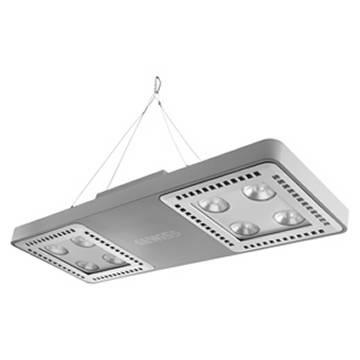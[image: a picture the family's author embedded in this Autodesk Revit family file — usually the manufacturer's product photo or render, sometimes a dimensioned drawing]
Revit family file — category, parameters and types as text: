
# Revit family: Lighting-Industrial-GEWISS-SMART[4]HE_HIGHBAYS-LED_2M_DALI
name_source: partatom
category: Apparecchi per illuminazione
units: mm (PartAtom-declared; Revit-internal decimal feet)

## family parameters
Basato su piano di lavoro = Sì
Condiviso = No
Numero OmniClass = 23.80.70.00
Punto di calcolo locali = No
Quota connettore circolare = Usa diametro
Sempre verticale = No
Sorgente d'illuminazione = No
Taglio con vuoti quando caricato = No
Tipo di parte = Normale
Titolo OmniClass = Lighting

## types (36) — shared parameters
Application = Internal
Body = PA6 "Halogen Free" loaded fibreglass
Carico apparente = 97 VA
Catalogue = LIGHTING
Classification: = -
Classificazione = Lighting
Color Rendering Index = CRI-80
Colour = Grey RAL 7035
Colour : = Grey RAL 7035
Commenti sul wattaggio = 97W
Context = Lighting for industries and sports facilities
Control System = 1 x DALI DT6
Control System : = DALI
DIN 18032-3 certification = With Bracket - Rope Kit + terminal&nbsp;(in approval)
Device with reduced surface temperature = Yes
Dist_sorg_lum = 10 mm  [stored 0.0328084 ft]
Driver = Included
Driver Box = Built-in
Electrocod = 2444
Eletrical and lighting features = -
External screw = Stainless steel
Fixing = -
Gasket = anti-aging silicone
General information = -
Glow Wire Test : = 850 °C
IDF = 71863346-6837-4260-98ca-c6d85b474ae1
IDT = 32167967fdf74962832821affbd5ec12
IP degree = IP66
IPEA = -
Immagine tipo = GWL1311.jpg
Installationa and maintenance = -
Insulation class = I
LED Maintenance = Non-replaceable
Lampada = LED
Larghezza = 254 mm
Lifetime = L90B10 (Tq+25°C) = 100.000 h - L90B10 (Tq+50°C) = 50.000 h
Locking Hook = -
Luminaire = LED Industrial ReflectorÂ
Lunghezza = 699 mm  [stored 2.29331 ft]
Mascherina = <Per categoria>
Materials = -
Maximum surface exposed to the wind : = 0,184 m²
Motore = <Per categoria>
Mouting and installation = Ceiling - Wallmounting - Suspension
Operating temperature : = -30°C ÷ +50 °C
Optic Maintenance = Non-replaceable
Optic and illuminating features = -
Overvoltage protection = DM 6 kV / CM 10 kV
Photobiological Risk Class = RG0
Produttore = GEWISS S.p.A.
Prospetto di default = 1219 mm
Rated frequency (Hz) = 50/60 Hz
Shield type = Tempered glass Thickness 4mm
Shock resistance = IK08
Spessore plafoniera = 40 mm  [stored 0.131234 ft]
Standard Deviation Colour Matching = SDCM = 3
Standard- = EN 60598-1 ; EN 60598-2-1 ; EN 60598-2-24
Standards and approvals = -
Stocking temperature = -40 +70 °C
Struttura plafoniera = <Per categoria>
Supply voltage = 220 - 240 V
System power = 95W
Technical sheet = https://www.gewiss.com
Tilt- = With bracket accessory
Trasformatore = <Per categoria>
Type of light source = LED - Not replaceable
URL = https://www.gewiss.com
Unique digital code (Datamatrix) = Datamatrix
Version file RFA = 20.11
Voltaggio = 230 V
Warranty = 5 years
Weight (kg): = 6,5
Wiring = With GW connect watertight connector

## per-type parameters (varying)
| type | Colour temperature | Descrizione | Efficiency (lm/W) | Lumen output (lm) | Modello | Optic | Optic : | SEO | Unified Glare Rating |
| GWS4223AC857 - SMART4HB 2M C.PAS.DALI ASI.57K | 5700K | SMART[4]HB 2M C.PAS.DALI ASI.57K | 132 | 12500 | GWS4223AC857 | Asymmetrical | Metallic PC reflector and PMMA lenses | High bay | - |
| GWS4223AF857 - SMART4HB 2M C.PAS.DALI 30° 57K | 5700K | SMART[4]HB 2M C.PAS.DALI 30° 57K | 144 | 13700 | GWS4223AF857 | 30° | Metallic PC reflector and PMMA lenses |  | UGR - 19 |
| GWS4221AF830 - SMART4HB 2M ST.AL.DALI 30° 30K | 3000K | SMART[4]HB 2M ST.AL.DALI 30° 30K | 137 | 13000 | GWS4221AF830 | 30° | Metallic PC reflector and PMMA lenses |  | UGR - 19 |
| GWS4221AH830 - SMART4HB 2M ST.AL.DALI 60° 30K | 3000K | SMART[4]HB 2M ST.AL.DALI 60° 30K | 138 | 13100 | GWS4221AH830 | 60° | Metallic PC reflector and PMMA lenses |  | UGR - 22 |
| GWS4221AA857 - SMART4HB 2M ST.AL.DALI ARR.57K | 5700K | SMART[4]HB 2M ST.AL.DALI ARR.57K | 145 | 13800 | GWS4221AA857 | Array | Metallized polycarbonate reflector |  | UGR - 25 |
| GWS4223AP840 - SMART4HB 2M C.PAS.DALI 90° 40K | 4000K | SMART[4]HB 2M C.PAS.DALI 90° 40K | 146 | 13900 | GWS4223AP840 | 90° | Metallic PC reflector and PMMA lenses |  | UGR - 22 |
| GWS4221AP857 - SMART4HB 2M ST.AL.DALI 90° 57K | 5700K | SMART[4]HB 2M ST.AL.DALI 90° 57K | 146 | 13900 | GWS4221AP857 | 90° | Metallic PC reflector and PMMA lenses |  | UGR - 22 |
| GWS4223AQ830 - SMART4HB 2M C.PAS.DALI ELL.30K | 3000K | SMART[4]HB 2M C.PAS.DALI ELL.30K | 124 | 11800 | GWS4223AQ830 | Elliptical | Metallic PC reflector and PMMA lenses | High bay | - |
| GWS4223AC840 - SMART4HB 2M C.PAS.DALI ASI.40K | 4000K | SMART[4]HB 2M C.PAS.DALI ASI.40K | 132 | 12500 | GWS4223AC840 | Asymmetrical | Metallic PC reflector and PMMA lenses | High bay | - |
| GWS4223AF830 - SMART4HB 2M C.PAS.DALI 30° 30K | 3000K | SMART[4]HB 2M C.PAS.DALI 30° 30K | 137 | 13000 | GWS4223AF830 | 30° | Metallic PC reflector and PMMA lenses |  | UGR - 19 |
| GWS4221AA840 - SMART4HB 2M ST.AL.DALI ARR.40K | 4000K | SMART[4]HB 2M ST.AL.DALI ARR.40K | 145 | 13800 | GWS4221AA840 | Array | Metallized polycarbonate reflector |  | UGR - 25 |
| GWS4223AA830 - SMART4HB 2M C.PAS.DALI ARR.30K | 3000K | SMART[4]HB 2M C.PAS.DALI ARR.30K | 139 | 13200 | GWS4223AA830 | Array | Metallized polycarbonate reflector |  | UGR - 25 |
| GWS4221AA830 - SMART4HB 2M ST.AL.DALI ARR.30K | 3000K | SMART[4]HB 2M ST.AL.DALI ARR.30K | 139 | 13200 | GWS4221AA830 | Array | Metallized polycarbonate reflector |  | UGR - 25 |
| GWS4223AH830 - SMART4HB 2M C.PAS.DALI 60° 30K | 3000K | SMART[4]HB 2M C.PAS.DALI 60° 30K | 138 | 13100 | GWS4223AH830 | 60° | Metallic PC reflector and PMMA lenses |  | UGR - 22 |
| GWS4223AH840 - SMART4HB 2M C.PAS.DALI 60° 40K | 4000K | SMART[4]HB 2M C.PAS.DALI 60° 40K | 145 | 13800 | GWS4223AH840 | 60° | Metallic PC reflector and PMMA lenses |  | UGR - 22 |
| GWS4221AQ830 - SMART4HB 2M ST.AL.DALI ELL.30K | 3000K | SMART[4]HB 2M ST.AL.DALI ELL.30K | 124 | 11800 | GWS4221AQ830 | Elliptical | Metallic PC reflector and PMMA lenses | High bay | - |
| GWS4223AF840 - SMART4HB 2M C.PAS.DALI 30° 40K | 4000K | SMART[4]HB 2M C.PAS.DALI 30° 40K | 144 | 13700 | GWS4223AF840 | 30° | Metallic PC reflector and PMMA lenses |  | UGR - 19 |
| GWS4223AP830 - SMART4HB 2M C.PAS.DALI 90° 30K | 3000K | SMART[4]HB 2M C.PAS.DALI 90° 30K | 140 | 13300 | GWS4223AP830 | 90° | Metallic PC reflector and PMMA lenses |  | UGR - 22 |
| GWS4223AC830 - SMART4HB 2M C.PAS.DALI ASI.30K | 3000K | SMART[4]HB 2M C.PAS.DALI ASI.30K | 125 | 11900 | GWS4223AC830 | Asymmetrical | Metallic PC reflector and PMMA lenses | High bay | - |
| GWS4221AQ857 - SMART4HB 2M ST.AL.DALI ELL.57K | 5700K | SMART[4]HB 2M ST.AL.DALI ELL.57K | 129 | 12300 | GWS4221AQ857 | Elliptical | Metallic PC reflector and PMMA lenses | High bay | - |
| GWS4221AH857 - SMART4HB 2M ST.AL.DALI 60° 57K | 5700K | SMART[4]HB 2M ST.AL.DALI 60° 57K | 145 | 13800 | GWS4221AH857 | 60° | Metallic PC reflector and PMMA lenses |  | UGR - 22 |
| GWS4221AP830 - SMART4HB 2M ST.AL.DALI 90° 30K | 3000K | SMART[4]HB 2M ST.AL.DALI 90° 30K | 140 | 13300 | GWS4221AP830 | 90° | Metallic PC reflector and PMMA lenses |  | UGR - 22 |
| GWS4221AC857 - SMART4HB 2M ST.AL.DALI ASI.57K | 5700K | SMART[4]HB 2M ST.AL.DALI ASI.57K | 132 | 12500 | GWS4221AC857 | Asymmetrical | Metallic PC reflector and PMMA lenses | High bay | - |
| GWS4221AF857 - SMART4HB 2M ST.AL.DALI 30° 57K | 5700K | SMART[4]HB 2M ST.AL.DALI 30° 57K | 144 | 13700 | GWS4221AF857 | 30° | Metallic PC reflector and PMMA lenses |  | UGR - 19 |
| GWS4223AH857 - SMART4HB 2M C.PAS.DALI 60° 57K | 5700K | SMART[4]HB 2M C.PAS.DALI 60° 57K | 145 | 13800 | GWS4223AH857 | 60° | Metallic PC reflector and PMMA lenses |  | UGR - 22 |
| GWS4221AQ840 - SMART4HB 2M ST.AL.DALI ELL.40K | 4000K | SMART[4]HB 2M ST.AL.DALI ELL.40K | 129 | 12300 | GWS4221AQ840 | Elliptical | Metallic PC reflector and PMMA lenses | High bay | - |
| GWS4221AC840 - SMART4HB 2M ST.AL.DALI ASI.40K | 4000K | SMART[4]HB 2M ST.AL.DALI ASI.40K | 132 | 12500 | GWS4221AC840 | Asymmetrical | Metallic PC reflector and PMMA lenses | High bay | - |
| GWS4221AF840 - SMART4HB 2M ST.AL.DALI 30° 40K | 4000K | SMART[4]HB 2M ST.AL.DALI 30° 40K | 144 | 13700 | GWS4221AF840 | 30° | Metallic PC reflector and PMMA lenses |  | UGR - 19 |
| GWS4221AP840 - SMART4HB 2M ST.AL.DALI 90° 40K | 4000K | SMART[4]HB 2M ST.AL.DALI 90° 40K | 146 | 13900 | GWS4221AP840 | 90° | Metallic PC reflector and PMMA lenses |  | UGR - 22 |
| GWS4223AQ857 - SMART4HB 2M C.PAS.DALI ELL.57K | 5700K | SMART[4]HB 2M C.PAS.DALI ELL.57K | 129 | 12300 | GWS4223AQ857 | Elliptical | Metallic PC reflector and PMMA lenses | High bay | - |
| GWS4221AH840 - SMART4HB 2M ST.AL.DALI 60° 40K | 4000K | SMART[4]HB 2M ST.AL.DALI 60° 40K | 145 | 13800 | GWS4221AH840 | 60° | Metallic PC reflector and PMMA lenses |  | UGR - 22 |
| GWS4221AC830 - SMART4HB 2M ST.AL.DALI ASI.30K | 3000K | SMART[4]HB 2M ST.AL.DALI ASI.30K | 125 | 11900 | GWS4221AC830 | Asymmetrical | Metallic PC reflector and PMMA lenses | High bay | - |
| GWS4223AQ840 - SMART4HB 2M C.PAS.DALI ELL.40K | 4000K | SMART[4]HB 2M C.PAS.DALI ELL.40K | 129 | 12300 | GWS4223AQ840 | Elliptical | Metallic PC reflector and PMMA lenses | High bay | - |
| GWS4223AP857 - SMART4HB 2M C.PAS.DALI 90° 57K | 5700K | SMART[4]HB 2M C.PAS.DALI 90° 57K | 146 | 13900 | GWS4223AP857 | 90° | Metallic PC reflector and PMMA lenses |  | UGR - 22 |
| GWS4223AA857 - SMART4HB 2M C.PAS.DALI ARR.57K | 5700K | SMART[4]HB 2M C.PAS.DALI ARR.57K | 145 | 13800 | GWS4223AA857 | Array | Metallized polycarbonate reflector |  | UGR - 25 |
| GWS4223AA840 - SMART4HB 2M C.PAS.DALI ARR.40K | 4000K | SMART[4]HB 2M C.PAS.DALI ARR.40K | 145 | 13800 | GWS4223AA840 | Array | Metallized polycarbonate reflector |  | UGR - 25 |

note: [stored X ft] marks values corroborated as IEEE doubles in the binary element streams (Revit-internal decimal feet)

## geometry (parser evidence)
native form markers: Blend x4, Sweep x3
no freeform markers — native parametric forms only
